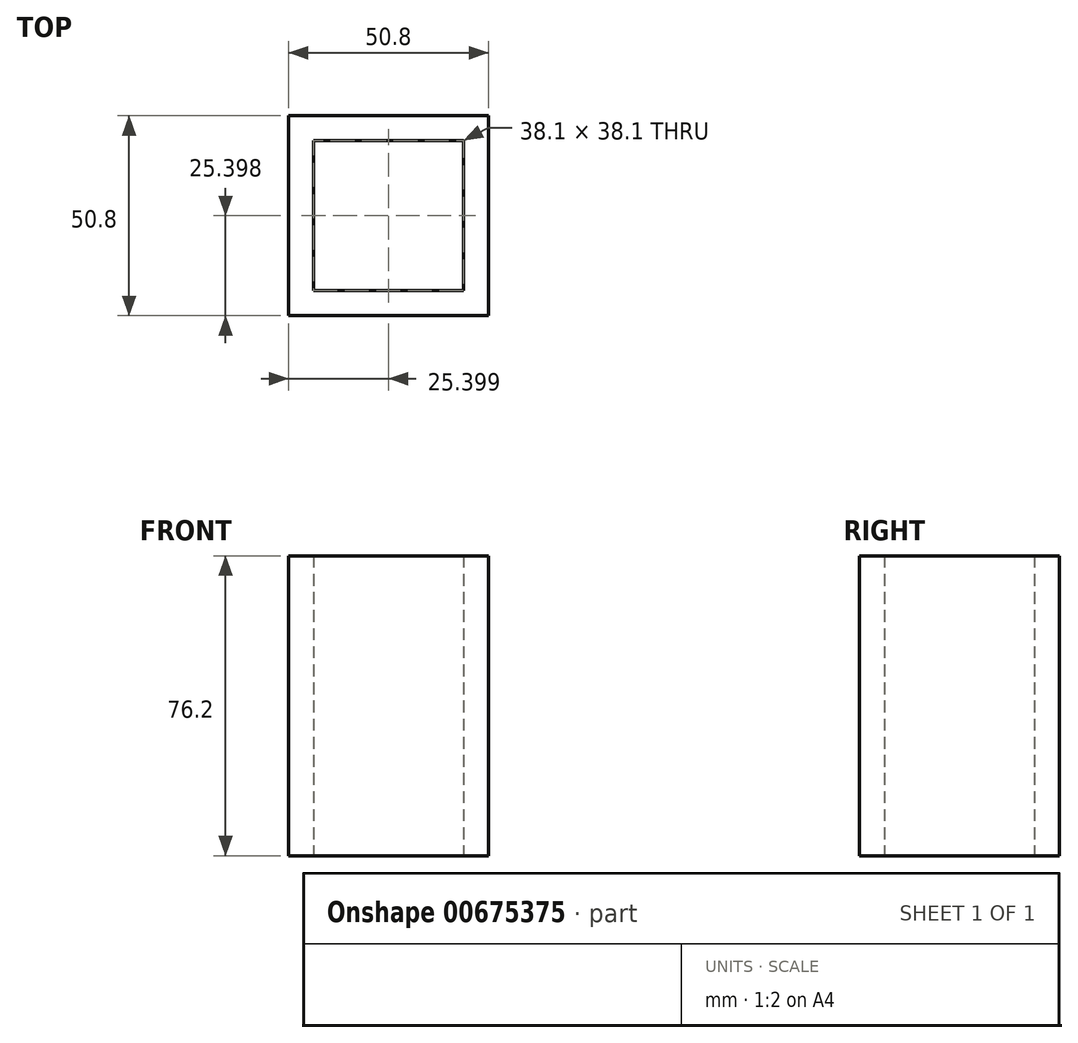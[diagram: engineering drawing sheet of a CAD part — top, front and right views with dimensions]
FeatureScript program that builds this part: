
annotation { "Feature Type Name" : "Feature", "Feature Type Description" : "" }
export const myFeature = defineFeature(function(context is Context, id is Id, definition is map)
    precondition{}
    {
        {
            var Q0;
            Q0=qCreatedBy(makeId("Top.planeOp"),FACE);
            var sketch = newSketch(context, id + "F0", { "sketchPlane" : qUnion([Q0])});
            skLineSegment(sketch, "E0.bottom", {"start": v(-19.17, 25.67) * mm, "end": v(31.63, 25.67) * mm});
            skLineSegment(sketch, "E0.top", {"start": v(-19.17, -25.13) * mm, "end": v(31.63, -25.13) * mm});
            skLineSegment(sketch, "E0.left", {"start": v(-19.17, 25.67) * mm, "end": v(-19.17, -25.13) * mm});
            skLineSegment(sketch, "E0.right", {"start": v(31.63, 25.67) * mm, "end": v(31.63, -25.13) * mm});
            skLineSegment(sketch, "E1.bottom", {"start": v(-12.82, 19.32) * mm, "end": v(25.28, 19.32) * mm});
            skLineSegment(sketch, "E1.top", {"start": v(-12.82, -18.78) * mm, "end": v(25.28, -18.78) * mm});
            skLineSegment(sketch, "E1.left", {"start": v(-12.82, 19.32) * mm, "end": v(-12.82, -18.78) * mm});
            skLineSegment(sketch, "E1.right", {"start": v(25.28, 19.32) * mm, "end": v(25.28, -18.78) * mm});
            skSolve(sketch);
        }
        {
            var Q0;
            Q0=makeQuery(id+"F0.imprint","IMPRINT",FACE,{"disambiguationData":[TD([[makeQuery(id+"F0.imprint","IMPRINT",EDGE,{"derivedFrom":sQuery(id+"F0.wireOp",EDGE,"E0.bottom")}),-1.0]])]});
            extrude(context, id + "F1", {"entities" : qUnion([Q0]), "depth" : 76.2 * mm, "offsetDistance" : 25.4 * mm});
        }
    });
